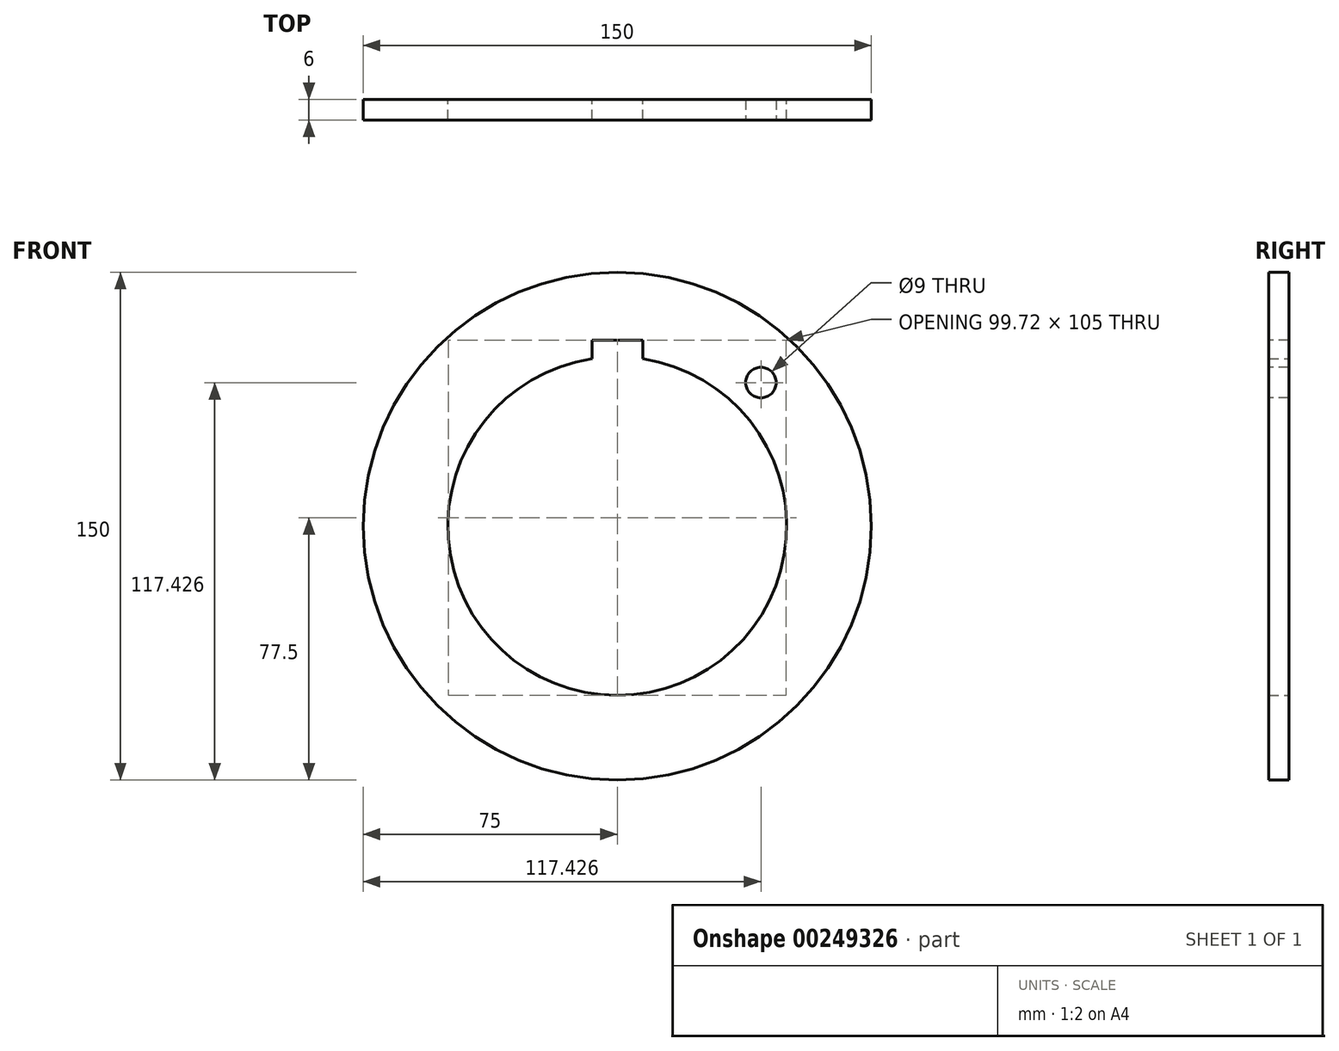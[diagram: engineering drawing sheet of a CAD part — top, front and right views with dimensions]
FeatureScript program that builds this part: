
annotation { "Feature Type Name" : "Feature", "Feature Type Description" : "" }
export const myFeature = defineFeature(function(context is Context, id is Id, definition is map)
    precondition{}
    {
        {
            var Q0;
            Q0=qCreatedBy(makeId("Top.planeOp"),FACE);
            var sketch = newSketch(context, id + "F0", { "sketchPlane" : qUnion([Q0])});
            skLineSegment(sketch, "E0", {"start": v(0, 0) * mm, "end": v(0, -70.33) * mm});
            skSolve(sketch);
        }
        {
            var Q0;
            Q0=qCreatedBy(makeId("Front.planeOp"),FACE);
            var sketch = newSketch(context, id + "F1", { "sketchPlane" : qUnion([Q0])});
            skCircle(sketch, "E1", {"center": v(0, 0) * mm, "radius": 75 * mm});
            skCircle(sketch, "E2", {"center": v(0, 0) * mm, "radius": 50 * mm});
            skSolve(sketch);
        }
        {
            var Q0;
            Q0=makeQuery(id+"F1.imprint","IMPRINT",FACE,{"disambiguationData":[TD([[makeQuery(id+"F1.imprint","IMPRINT",EDGE,{"derivedFrom":sQuery(id+"F1.wireOp",EDGE,"E1")}),1.0]])]});
            extrude(context, id + "F2", {"entities" : qUnion([Q0]), "depth" : 6 * mm, "symmetric" : true});
        }
        {
            var Q0;
            Q0=makeQuery(id+"F2.opExtrude","CAP_FACE",FACE,{"disambiguationData":[OSD([sQuery(id+"F1.wireOp",EDGE,"E1"),sQuery(id+"F1.wireOp",EDGE,"E2")])],"isStart":false});
            var sketch = newSketch(context, id + "F3", { "sketchPlane" : qUnion([Q0])});
            skLineSegment(sketch, "E3.bottom", {"start": v(-7.5, 0) * mm, "end": v(7.5, 0) * mm});
            skLineSegment(sketch, "E3.top", {"start": v(-7.5, 55) * mm, "end": v(7.5, 55) * mm});
            skLineSegment(sketch, "E3.left", {"start": v(-7.5, 0) * mm, "end": v(-7.5, 55) * mm});
            skLineSegment(sketch, "E3.right", {"start": v(7.5, 0) * mm, "end": v(7.5, 55) * mm});
            skSolve(sketch);
        }
        {
            var Q0;
            {var subQ0=sQuery(id+"F3.wireOp",EDGE,"E3.bottom");Q0=makeQuery(id+"F3.imprint","IMPRINT",FACE,{"disambiguationData":[TD([[makeQuery(id+"F3.imprint","IMPRINT",EDGE,{"derivedFrom":subQ0}),1.0]])]});}
            var Q1;
            {var subQ0=sQuery(id+"F3.wireOp",EDGE,"E3.top");Q1=makeQuery(id+"F3.imprint","IMPRINT",FACE,{"disambiguationData":[TD([[makeQuery(id+"F3.imprint","IMPRINT",EDGE,{"derivedFrom":subQ0}),-1.0]])]});}
            extrude(context, id + "F4", {"entities" : qUnion([Q0, Q1]), "operationType" : NewBodyOperationType.REMOVE, "oppositeDirection" : true, "depth" : 35 * mm});
        }
        {
            var Q0;
            Q0=qCreatedBy(makeId("Front.planeOp"),FACE);
            var sketch = newSketch(context, id + "F5", { "sketchPlane" : qUnion([Q0])});
            skLineSegment(sketch, "E4", {"start": v(0, 0) * mm, "end": v(42.43, 42.43) * mm, "construction": true});
            skCircle(sketch, "E5", {"center": v(42.43, 42.43) * mm, "radius": 4.5 * mm});
            skSolve(sketch);
        }
        {
            var Q0;
            Q0 = qSketchRegion(id + "F5", true);
            extrude(context, id + "F6", {"entities" : qUnion([Q0]), "operationType" : NewBodyOperationType.REMOVE, "oppositeDirection" : true, "depth" : 25 * mm, "symmetric" : true});
        }
    });
